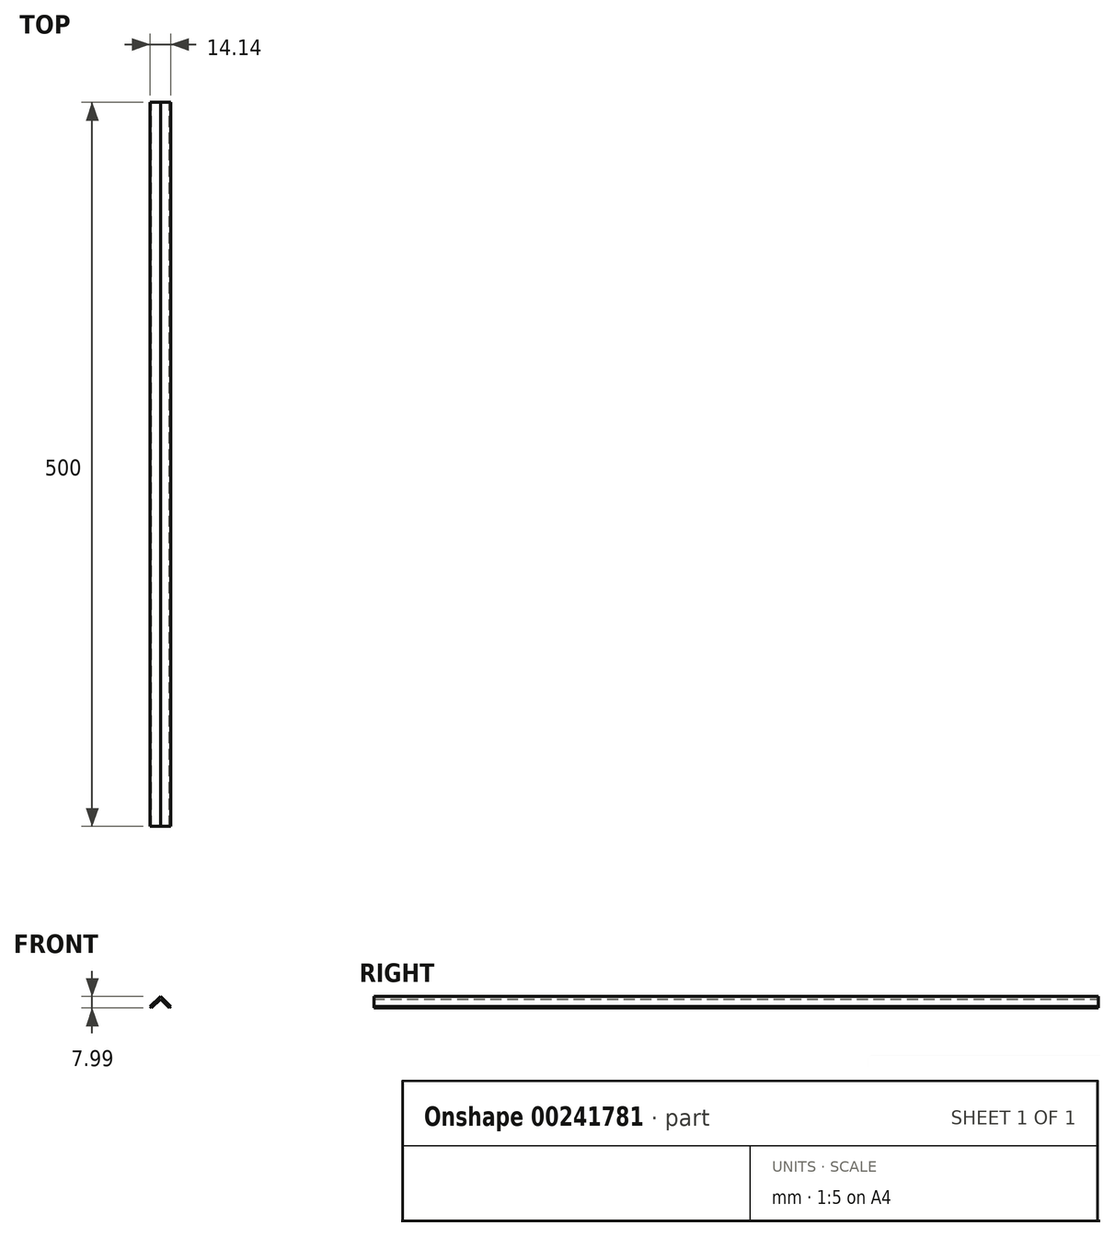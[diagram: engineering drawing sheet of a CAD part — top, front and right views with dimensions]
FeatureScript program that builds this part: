
annotation { "Feature Type Name" : "Feature", "Feature Type Description" : "" }
export const myFeature = defineFeature(function(context is Context, id is Id, definition is map)
    precondition{}
    {
        {
            var Q0;
            Q0=qCreatedBy(makeId("Front.planeOp"),FACE);
            var sketch = newSketch(context, id + "F0", { "sketchPlane" : qUnion([Q0])});
            skLineSegment(sketch, "E0", {"start": v(0, 0) * mm, "end": v(7.07, 7.07) * mm});
            skLineSegment(sketch, "E1", {"start": v(7.07, 7.07) * mm, "end": v(14.14, 0) * mm});
            skLineSegment(sketch, "E2", {"start": v(14.14, 0) * mm, "end": v(13.22, -0.92) * mm});
            skLineSegment(sketch, "E3", {"start": v(13.22, -0.92) * mm, "end": v(7.07, 5.23) * mm});
            skLineSegment(sketch, "E4", {"start": v(7.07, 5.23) * mm, "end": v(0.92, -0.92) * mm});
            skLineSegment(sketch, "E5", {"start": v(0.92, -0.92) * mm, "end": v(0, 0) * mm});
            skSolve(sketch);
        }
        {
            var Q0;
            Q0=qSketchRegion(id+"F0",true);
            extrude(context, id + "F1", {"entities" : qUnion([Q0]), "depth" : 500 * mm});
        }
    });
